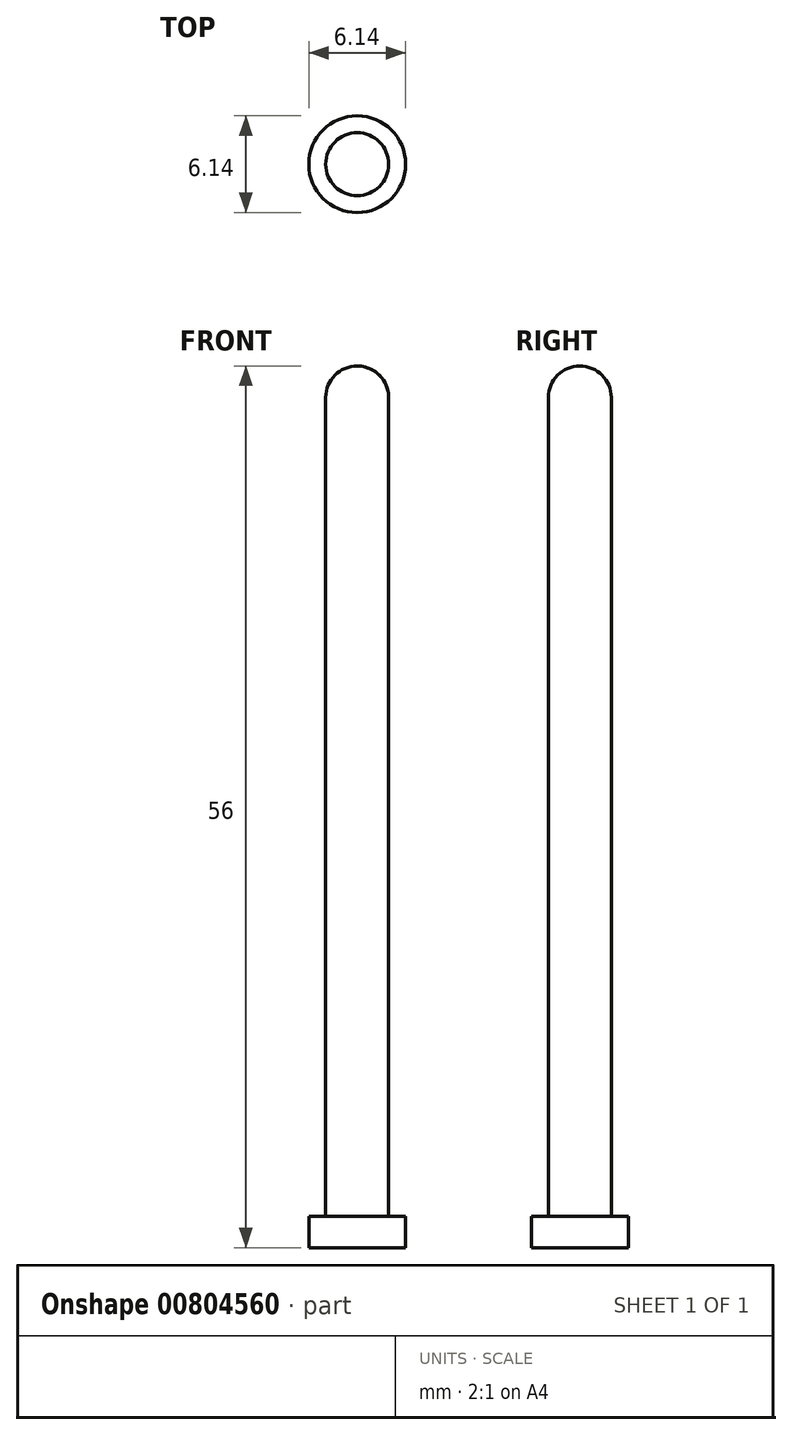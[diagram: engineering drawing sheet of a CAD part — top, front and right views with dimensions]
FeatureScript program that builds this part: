
annotation { "Feature Type Name" : "Feature", "Feature Type Description" : "" }
export const myFeature = defineFeature(function(context is Context, id is Id, definition is map)
    precondition{}
    {
        {
            var Q0;
            Q0=qCreatedBy(makeId("Top.planeOp"),FACE);
            var sketch = newSketch(context, id + "F0", { "sketchPlane" : qUnion([Q0])});
            skCircle(sketch, "E0", {"center": v(0, 0) * mm, "radius": 2 * mm});
            skCircle(sketch, "E1", {"center": v(0, 0) * mm, "radius": 3.07 * mm});
            skSolve(sketch);
        }
        {
            var Q0;
            Q0=makeQuery(id+"F0.imprint","IMPRINT",FACE,{"disambiguationData":[TD([[makeQuery(id+"F0.imprint","IMPRINT",EDGE,{"derivedFrom":sQuery(id+"F0.wireOp",EDGE,"E0")}),1.0]])]});
            extrude(context, id + "F1", {"entities" : qUnion([Q0]), "depth" : 56 * mm, "offsetDistance" : 25 * mm});
        }
        {
            var Q0;
            Q0 = qSketchRegion(id + "F0", true);
            var Q1;
            Q1=makeQuery(id+"F1.opExtrude","CAP_FACE",FACE,{"disambiguationData":[OSD([sQuery(id+"F0.wireOp",EDGE,"E0")])],"isStart":true});
            extrude(context, id + "F2", {"entities" : qUnion([Q0, Q1]), "operationType" : NewBodyOperationType.ADD, "depth" : 2 * mm, "offsetDistance" : 25 * mm});
        }
        {
            var Q0;
            Q0=makeQuery(id+"F1.opExtrude","CAP_EDGE",EDGE,{"disambiguationData":[OSD([sQuery(id+"F0.wireOp",EDGE,"E0")])],"isStart":false});
            fillet(context, id + "F3", {"entities" : qUnion([Q0]), "tangentPropagation" : true, "radius" : 2 * mm, "defaultsChanged" : true, "vertexSettings" : [], "allowEdgeOverflow" : false});
        }
    });
